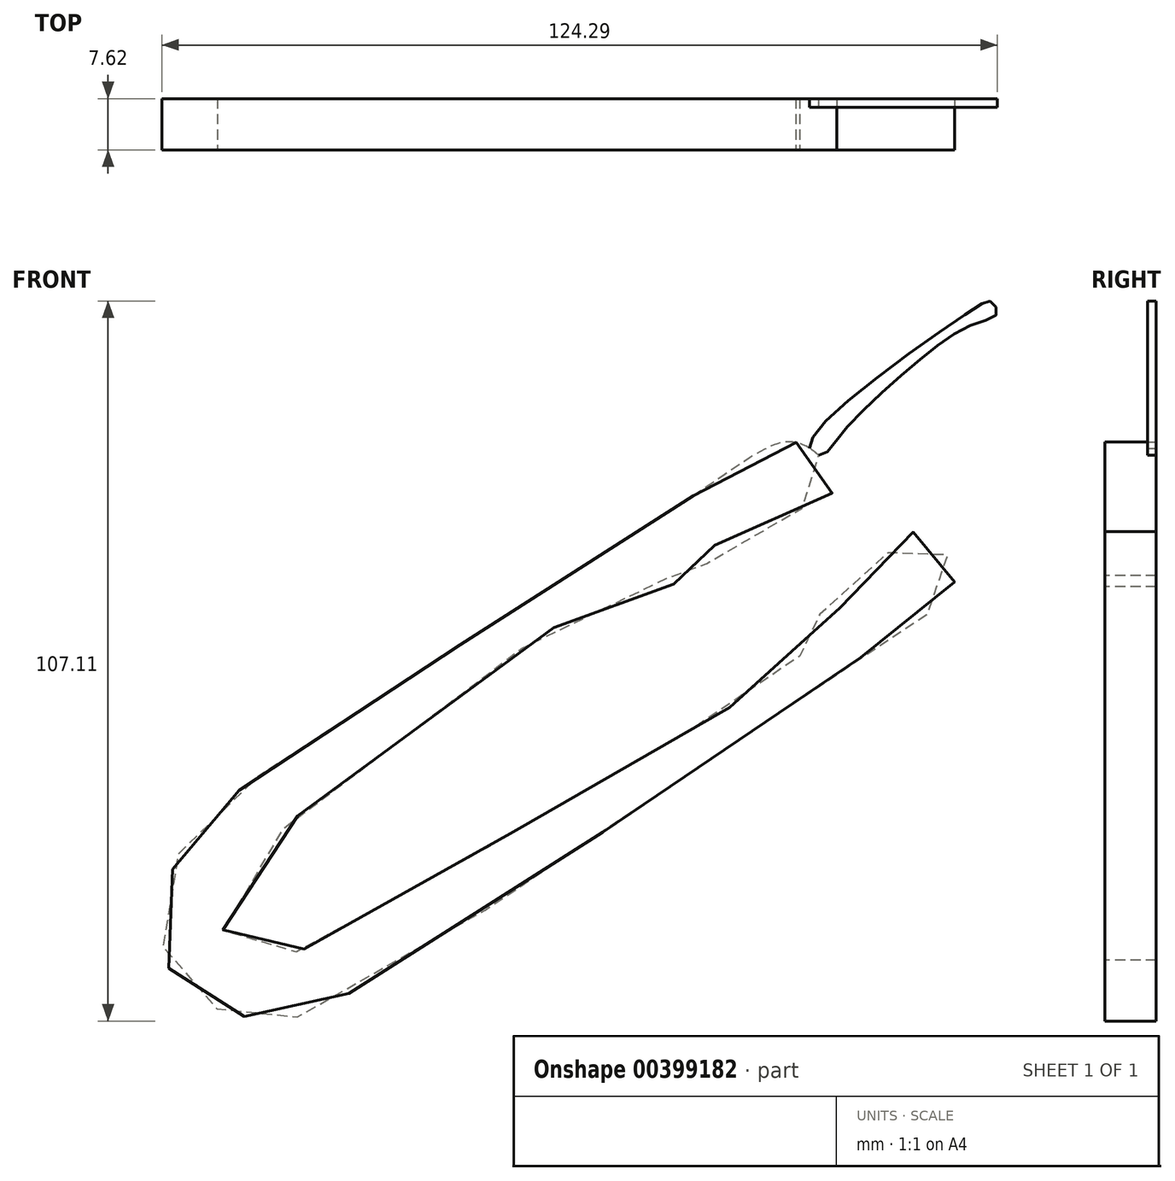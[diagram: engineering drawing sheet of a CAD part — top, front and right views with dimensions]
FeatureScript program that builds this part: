
annotation { "Feature Type Name" : "Feature", "Feature Type Description" : "" }
export const myFeature = defineFeature(function(context is Context, id is Id, definition is map)
    precondition{}
    {
        {
            var Q0;
            Q0=qCreatedBy(makeId("Front.planeOp"),FACE);
            var sketch = newSketch(context, id + "F0", { "sketchPlane" : qUnion([Q0])});
            skFitSpline(sketch, "E0", {"points": [v(10.82, 45.07) * mm, v(-58.52, 0) * mm, v(-66, -8.74) * mm, v(-68.22, -20.38) * mm, v(-64.34, -28.98) * mm, v(-54.91, -32.59) * mm, v(-44.93, -31.2) * mm, v(38.55, 22.88) * mm, v(49.64, 32.03) * mm, v(47.98, 37.3) * mm, v(42.99, 39.52) * mm, v(33.56, 28.98) * mm, v(28.01, 26.76) * mm, v(26.07, 22.88) * mm, v(26.62, 20.94) * mm, v(-2.5, 3.19) * mm, v(-54.08, -23.99) * mm, v(-58.8, -20.1) * mm, v(-58.52, -13.17) * mm, v(4.71, 33.14) * mm, v(7.77, 32.03) * mm, v(11.93, 32.3) * mm, v(14.14, 37.86) * mm, v(31.62, 45.62) * mm, v(30.5, 50.06) * mm, v(25.51, 53.1) * mm, v(10.82, 45.07) * mm]});
            skSolve(sketch);
        }
        {
            var Q0;
            Q0=qCreatedBy(makeId("Front.planeOp"),FACE);
            var sketch = newSketch(context, id + "F1", { "sketchPlane" : qUnion([Q0])});
            skSolve(sketch);
        }
        {
            var Q0;
            Q0 = qSketchRegion(id + "F1", true);
            var Q1;
            Q1=makeQuery(id+"F0.imprint","IMPRINT",FACE,{"disambiguationData":[TD([[makeQuery(id+"F0.imprint","IMPRINT",EDGE,{"derivedFrom":sQuery(id+"F0.wireOp",EDGE,"E0")}),1.0]])]});
            extrude(context, id + "F2", {"entities" : qUnion([Q0, Q1]), "depth" : 7.62 * mm});
        }
        {
            var Q0;
            Q0=qCreatedBy(makeId("Front.planeOp"),FACE);
            var sketch = newSketch(context, id + "F3", { "sketchPlane" : qUnion([Q0])});
            skFitSpline(sketch, "E1", {"points": [v(30.78, 56.44) * mm, v(53.25, 73.35) * mm, v(55.19, 73.9) * mm, v(56.02, 72.24) * mm, v(52.42, 70.58) * mm, v(43.82, 64.76) * mm, v(33, 54.5) * mm, v(29.95, 51.17) * mm, v(28.29, 51.72) * mm, v(30.78, 56.44) * mm]});
            skSolve(sketch);
        }
        {
            var Q0;
            Q0=makeQuery(id+"F3.imprint","IMPRINT",FACE,{"disambiguationData":[TD([[makeQuery(id+"F3.imprint","IMPRINT",EDGE,{"derivedFrom":sQuery(id+"F3.wireOp",EDGE,"E1")}),-1.0]])]});
            extrude(context, id + "F4", {"entities" : qUnion([Q0]), "operationType" : NewBodyOperationType.ADD, "depth" : 1.27 * mm});
        }
    });
